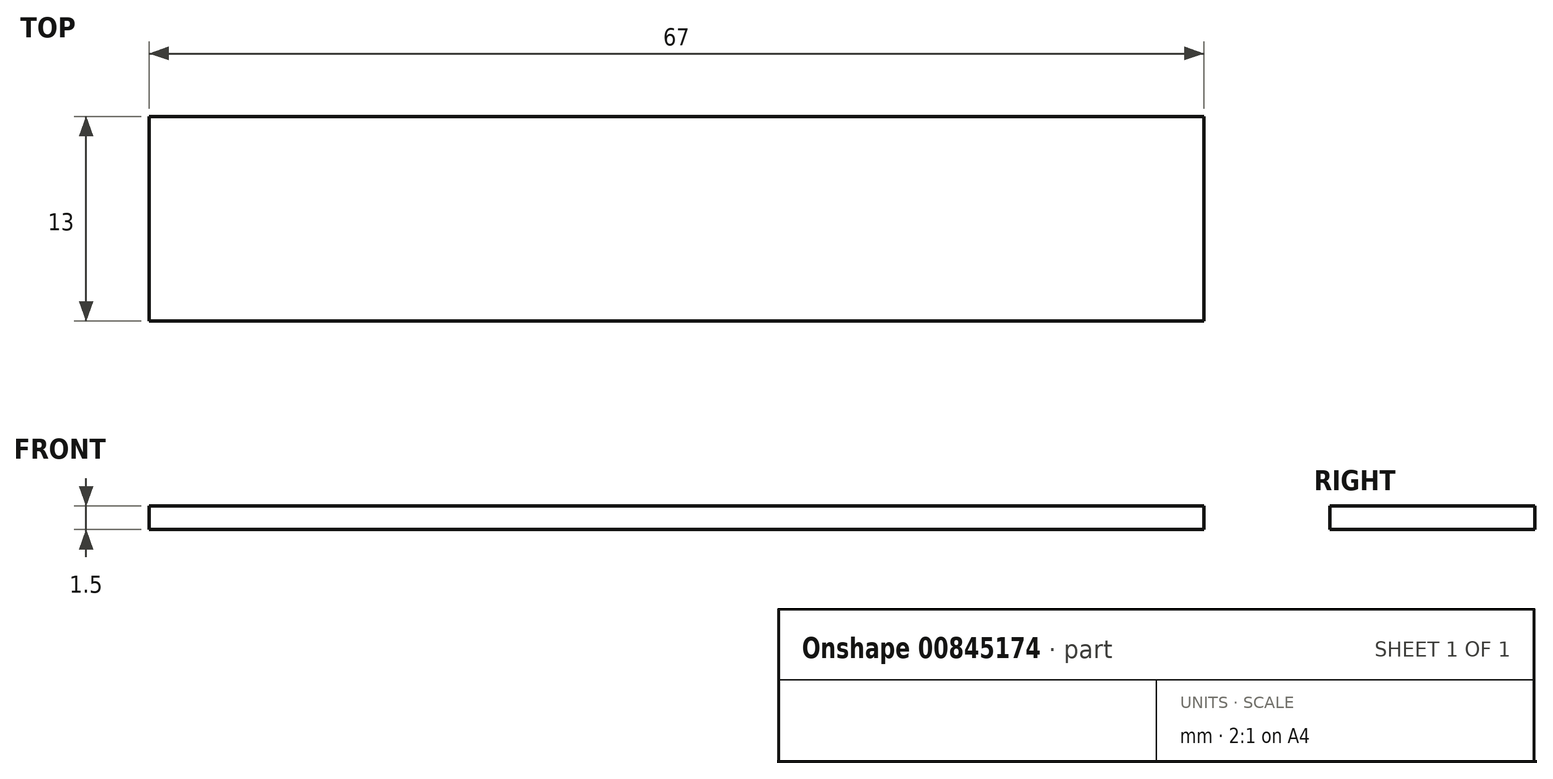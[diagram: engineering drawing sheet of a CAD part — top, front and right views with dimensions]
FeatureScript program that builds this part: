
annotation { "Feature Type Name" : "Feature", "Feature Type Description" : "" }
export const myFeature = defineFeature(function(context is Context, id is Id, definition is map)
    precondition{}
    {
        {
            var Q0;
            Q0=qCreatedBy(makeId("Top.planeOp"),FACE);
            var sketch = newSketch(context, id + "F0", { "sketchPlane" : qUnion([Q0])});
            skLineSegment(sketch, "E0.bottom", {"start": v(-33.5, -6.5) * mm, "end": v(33.5, -6.5) * mm});
            skLineSegment(sketch, "E0.top", {"start": v(-33.5, 6.5) * mm, "end": v(33.5, 6.5) * mm});
            skLineSegment(sketch, "E0.left", {"start": v(-33.5, -6.5) * mm, "end": v(-33.5, 6.5) * mm});
            skLineSegment(sketch, "E0.right", {"start": v(33.5, -6.5) * mm, "end": v(33.5, 6.5) * mm});
            skPoint(sketch, "E0.middle", {"position": v(0, 0) * mm});
            skSolve(sketch);
        }
        {
            var Q0;
            Q0=makeQuery(id+"F0.imprint","IMPRINT",FACE,{"disambiguationData":[TD([[makeQuery(id+"F0.imprint","IMPRINT",EDGE,{"derivedFrom":sQuery(id+"F0.wireOp",EDGE,"E0.bottom")}),1.0]])]});
            extrude(context, id + "F1", {"entities" : qUnion([Q0]), "depth" : 1.5 * mm, "offsetDistance" : 25 * mm});
        }
    });
